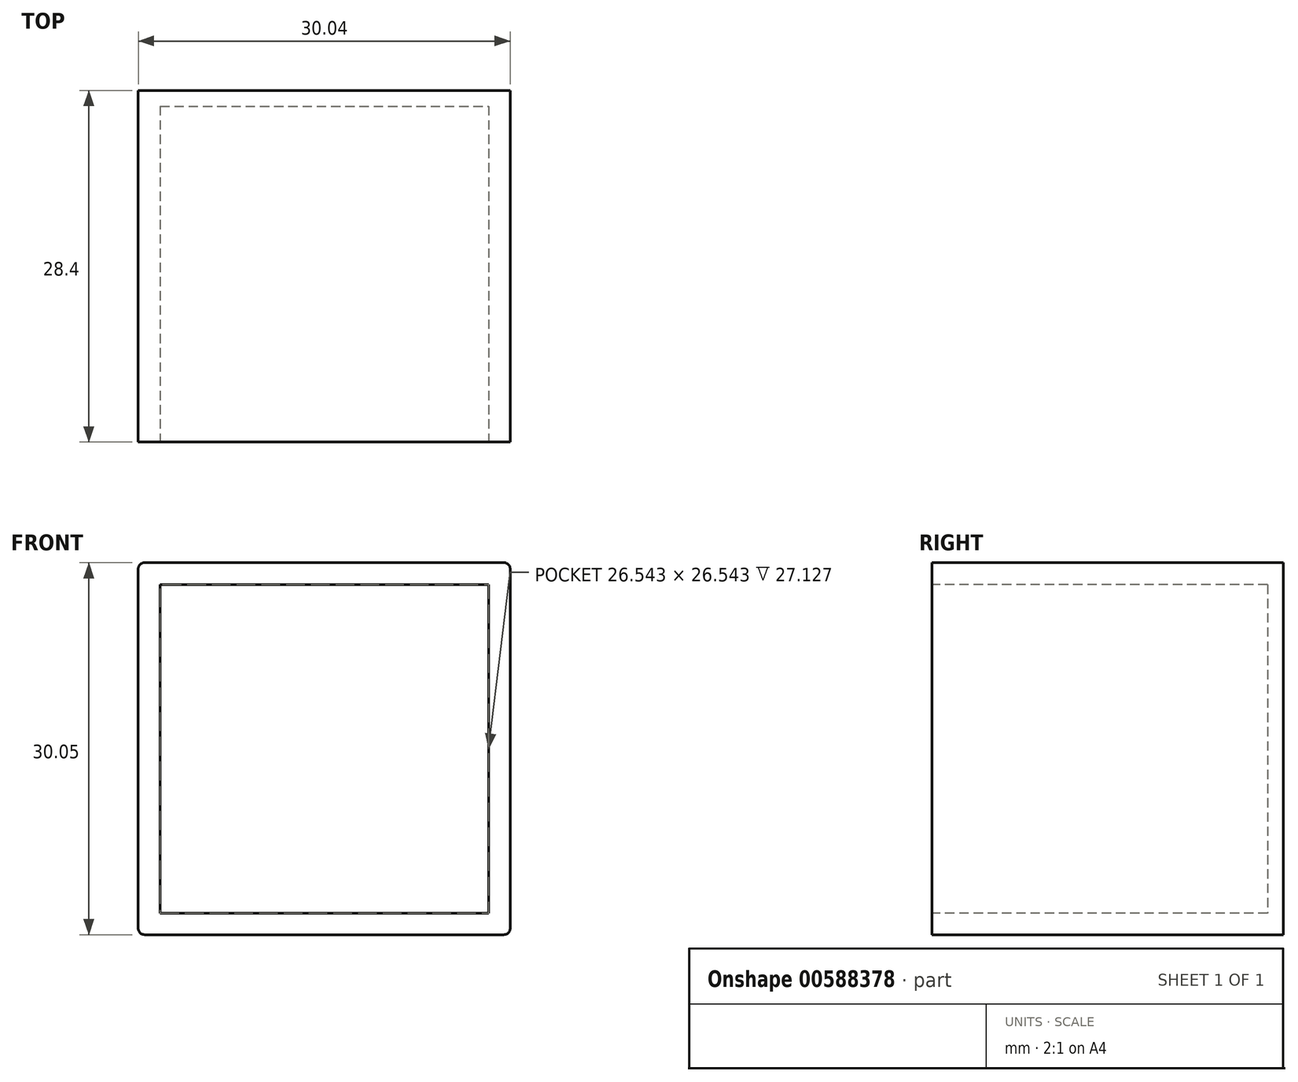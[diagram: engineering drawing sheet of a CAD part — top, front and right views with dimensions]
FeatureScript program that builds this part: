
annotation { "Feature Type Name" : "Feature", "Feature Type Description" : "" }
export const myFeature = defineFeature(function(context is Context, id is Id, definition is map)
    precondition{}
    {
        {
            var Q0;
            Q0=qCreatedBy(makeId("Front.planeOp"),FACE);
            var sketch = newSketch(context, id + "F0", { "sketchPlane" : qUnion([Q0])});
            skLineSegment(sketch, "E0.bottom", {"start": v(-13.24, 12.27) * mm, "end": v(16.8, 12.27) * mm});
            skLineSegment(sketch, "E0.top", {"start": v(-13.24, -17.78) * mm, "end": v(16.8, -17.78) * mm});
            skLineSegment(sketch, "E0.left", {"start": v(-13.24, 12.27) * mm, "end": v(-13.24, -17.78) * mm});
            skLineSegment(sketch, "E0.right", {"start": v(16.8, 12.27) * mm, "end": v(16.8, -17.78) * mm});
            skSolve(sketch);
        }
        {
            var Q0;
            Q0 = qSketchRegion(id + "F0", true);
            extrude(context, id + "F1", {"entities" : qUnion([Q0]), "depth" : 28.4 * mm, "offsetDistance" : 25.4 * mm});
        }
        {
            var Q0;
            Q0=makeQuery(id+"F1.opExtrude","CAP_FACE",FACE,{"disambiguationData":[OSD([sQuery(id+"F0.wireOp",EDGE,"E0.bottom"),sQuery(id+"F0.wireOp",EDGE,"E0.top"),sQuery(id+"F0.wireOp",EDGE,"E0.left"),sQuery(id+"F0.wireOp",EDGE,"E0.right")])],"isStart":false});
            var sketch = newSketch(context, id + "F2", { "sketchPlane" : qUnion([Q0])});
            skLineSegment(sketch, "E1.bottom", {"start": v(-11.47, 10.5) * mm, "end": v(15.08, 10.5) * mm});
            skLineSegment(sketch, "E1.top", {"start": v(-11.47, -16.05) * mm, "end": v(15.08, -16.05) * mm});
            skLineSegment(sketch, "E1.left", {"start": v(-11.47, 10.5) * mm, "end": v(-11.47, -16.05) * mm});
            skLineSegment(sketch, "E1.right", {"start": v(15.08, 10.5) * mm, "end": v(15.08, -16.05) * mm});
            skSolve(sketch);
        }
        {
            var Q0;
            Q0 = qSketchRegion(id + "F2", true);
            extrude(context, id + "F3", {"entities" : qUnion([Q0]), "operationType" : NewBodyOperationType.REMOVE, "oppositeDirection" : true, "depth" : 27.13 * mm, "offsetDistance" : 25.4 * mm});
        }
        {
            var Q0;
            Q0=makeQuery(id+"F1.opExtrude","SWEPT_EDGE",EDGE,{"disambiguationData":[OSD([sQuery(id+"F0.wireOp",EDGE,"E0.bottom"),sQuery(id+"F0.wireOp",EDGE,"E0.left")])]});
            var Q1;
            Q1=makeQuery(id+"F1.opExtrude","SWEPT_EDGE",EDGE,{"disambiguationData":[OSD([sQuery(id+"F0.wireOp",EDGE,"E0.top"),sQuery(id+"F0.wireOp",EDGE,"E0.left")])]});
            var Q2;
            Q2=makeQuery(id+"F1.opExtrude","SWEPT_EDGE",EDGE,{"disambiguationData":[OSD([sQuery(id+"F0.wireOp",EDGE,"E0.bottom"),sQuery(id+"F0.wireOp",EDGE,"E0.right")])]});
            var Q3;
            Q3=makeQuery(id+"F1.opExtrude","SWEPT_EDGE",EDGE,{"disambiguationData":[OSD([sQuery(id+"F0.wireOp",EDGE,"E0.top"),sQuery(id+"F0.wireOp",EDGE,"E0.right")])]});
            fillet(context, id + "F4", {"entities" : qUnion([Q0, Q1, Q2, Q3]), "radius" : 0.5 * mm, "tangentPropagation" : true, "allowEdgeOverflow" : false});
        }
    });
